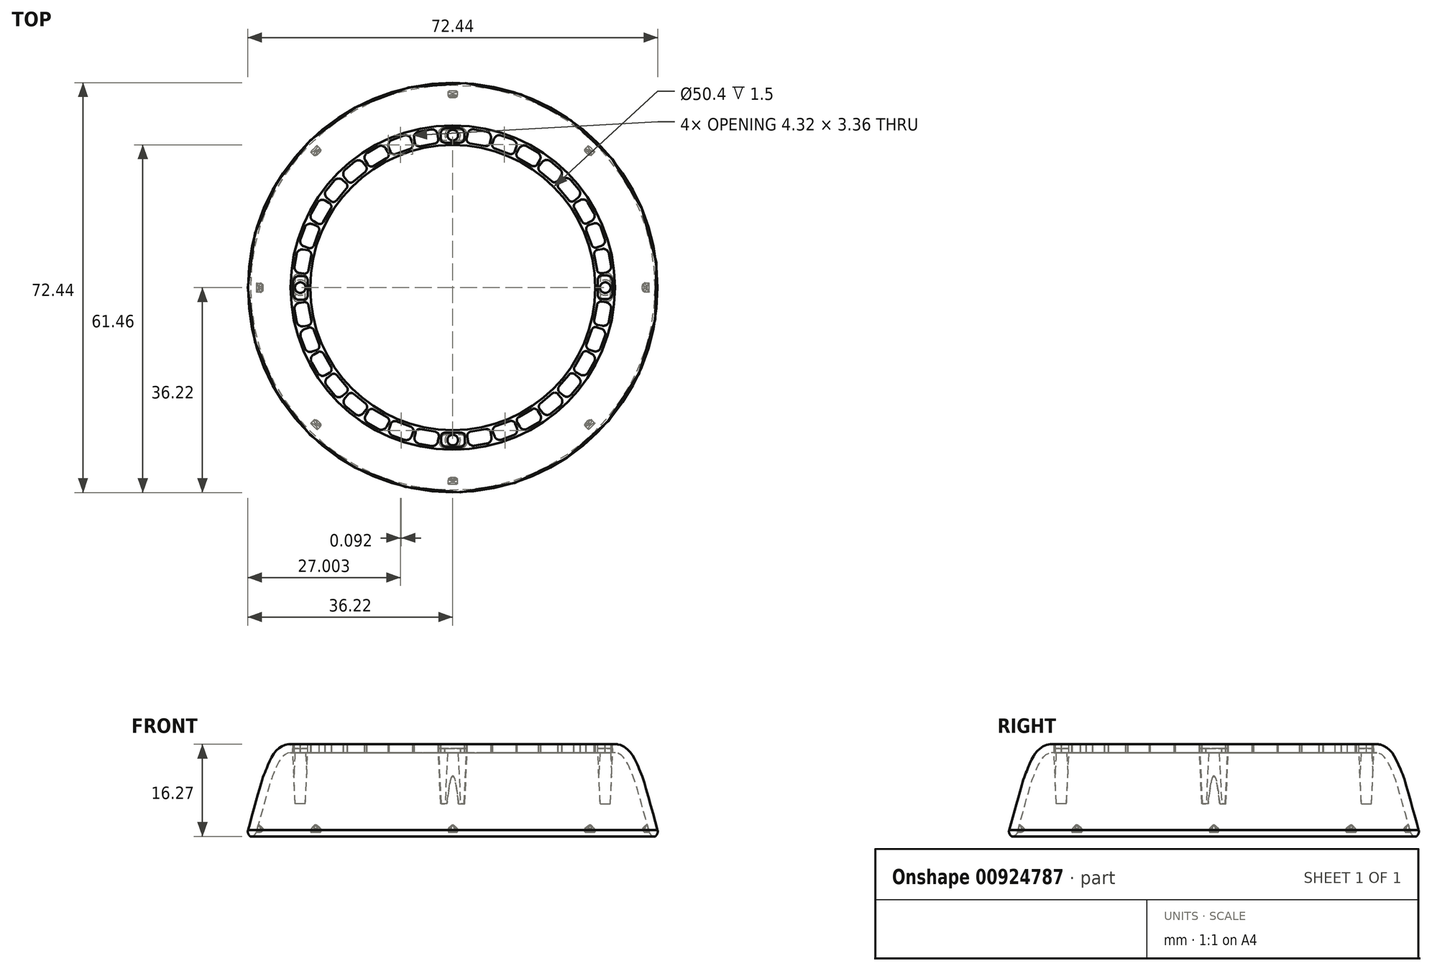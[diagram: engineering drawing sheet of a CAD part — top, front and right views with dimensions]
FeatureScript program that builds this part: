
annotation { "Feature Type Name" : "Feature", "Feature Type Description" : "" }
export const myFeature = defineFeature(function(context is Context, id is Id, definition is map)
    precondition{}
    {
        {
            var Q0;
            Q0=qCreatedBy(makeId("Front.planeOp"),FACE);
            var sketch = newSketch(context, id + "F0", { "sketchPlane" : qUnion([Q0])});
            skLineSegment(sketch, "E0", {"start": v(-25.2, 15) * mm, "end": v(-28.7, 15) * mm});
            skLineSegment(sketch, "E1", {"start": v(0, 0) * mm, "end": v(0, 15) * mm, "construction": true});
            skLineSegment(sketch, "E2", {"start": v(-25.2, 15) * mm, "end": v(0, 15) * mm, "construction": true});
            skLineSegment(sketch, "E3", {"start": v(0, 0) * mm, "end": v(-35, 0) * mm, "construction": true});
            skFitSpline(sketch, "E4", {"points": [v(-28.7, 15) * mm, v(-31.6, 11.48) * mm, v(-35, 0) * mm], "startDerivative": vector(-11.95, 0.53) * mm, "endDerivative": vector(-15.44, -55.66) * mm});
            skLineSegment(sketch, "E5", {"start": v(-25.2, 15) * mm, "end": v(-25.2, 0) * mm, "construction": true});
            skLineSegment(sketch, "E6", {"start": v(-25.2, 0) * mm, "end": v(-35, 0) * mm, "construction": true});
            skFitSpline(sketch, "E7.0", {"points": [v(-28.63, 16.5) * mm, v(-28.9, 16.51) * mm, v(-29.41, 16.46) * mm, v(-30.09, 16.2) * mm, v(-30.65, 15.85) * mm, v(-31.25, 15.3) * mm, v(-31.81, 14.54) * mm, v(-32.32, 13.61) * mm, v(-32.7, 12.75) * mm, v(-32.93, 12.16) * mm, v(-33.06, 11.85) * mm, v(-33.18, 11.58) * mm, v(-33.3, 11.3) * mm, v(-33.44, 10.94) * mm, v(-33.6, 10.49) * mm, v(-33.8, 9.88) * mm, v(-34.13, 8.7) * mm, v(-34.82, 6.27) * mm, v(-35.8, 2.72) * mm, v(-36.45, 0.4) * mm]});
            skLineSegment(sketch, "E7.1", {"start": v(-25.2, 16.5) * mm, "end": v(-28.67, 16.5) * mm});
            skLineSegment(sketch, "E8", {"start": v(-35.52, 0.14) * mm, "end": v(-36, 0.3) * mm});
            skLineSegment(sketch, "E9", {"start": v(-25.2, 16.5) * mm, "end": v(-25.2, 15) * mm});
            skArc(sketch, "E10.filletArc", {"start": v(-36, 0.3) * mm, "mid": v(-35.22, 0.36) * mm, "end": v(-34.73, 0.98) * mm});
            skPoint(sketch, "E11.visualSharp", {"position": v(-36.44, 0.43) * mm});
            skArc(sketch, "E11.filletArc", {"start": v(-36.18, 1.36) * mm, "mid": v(-36.1, 0.61) * mm, "end": v(-35.52, 0.14) * mm});
            skLineSegment(sketch, "E12", {"start": v(-25.2, 16.5) * mm, "end": v(0, 16.5) * mm, "construction": true});
            skLineSegment(sketch, "E13", {"start": v(0, 16.5) * mm, "end": v(0, 15) * mm, "construction": true});
            skLineSegment(sketch, "E14", {"start": v(-36.18, 1.36) * mm, "end": v(0, 1.36) * mm, "construction": true});
            skLineSegment(sketch, "E15.bottom", {"start": v(-25.7, 15) * mm, "end": v(-25.2, 15) * mm});
            skLineSegment(sketch, "E15.top", {"start": v(-25.45, 14.25) * mm, "end": v(-25.2, 14.25) * mm});
            skLineSegment(sketch, "E15.left", {"start": v(-25.7, 15) * mm, "end": v(-25.7, 14.5) * mm});
            skLineSegment(sketch, "E15.right", {"start": v(-25.2, 15) * mm, "end": v(-25.2, 14.25) * mm});
            skPoint(sketch, "E16.visualSharp", {"position": v(-25.7, 14.25) * mm});
            skArc(sketch, "E16.filletArc", {"start": v(-25.7, 14.5) * mm, "mid": v(-25.63, 14.32) * mm, "end": v(-25.45, 14.25) * mm});
            skSolve(sketch);
        }
        {
            var Q0;
            Q0=makeQuery(id+"F0.imprint","IMPRINT",FACE,{"disambiguationData":[TD([[makeQuery(id+"F0.imprint","IMPRINT",EDGE,{"derivedFrom":sQuery(id+"F0.wireOp",EDGE,"E0")}),-1.0]])]});
            var Q1;
            Q1=makeQuery(id+"F0.imprint","IMPRINT",FACE,{"disambiguationData":[TD([[makeQuery(id+"F0.imprint","IMPRINT",EDGE,{"derivedFrom":sQuery(id+"F0.wireOp",EDGE,"E15.bottom")}),-1.0]])]});
            var Q2;
            Q2=sQuery(id+"F0.wireOp",EDGE,"E1");
            revolve(context, id + "F1", {"surfaceOperationType" : NewSurfaceOperationType.NEW, "entities" : qUnion([Q0, Q1]), "axis" : qUnion([Q2]), "revolveType" : RevolveType.FULL});
        }
        {
            var Q0;
            Q0=sQuery(id+"F0.wireOp",VERTEX,"E1.end");
            var Q1;
            Q1=sQuery(id+"F0.wireOp",EDGE,"E1");
            cPlane(context, id + "F2", {"entities" : qUnion([Q0, Q1]), "cplaneType" : CPlaneType.LINE_POINT, "offset" : 25 * mm, "width" : 150 * mm, "height" : 150 * mm});
        }
        {
            var Q0;
            Q0=qCreatedBy(id+"F2.planeOp",FACE);
            var sketch = newSketch(context, id + "F3", { "sketchPlane" : qUnion([Q0])});
            skPoint(sketch, "E17.center", {"position": v(0, 0) * mm});
            skLineSegment(sketch, "E18.bottom", {"start": v(-27.26, -2.54) * mm, "end": v(-26.63, -2.54) * mm});
            skLineSegment(sketch, "E18.top", {"start": v(-27.26, 2.43) * mm, "end": v(-26.63, 2.43) * mm});
            skLineSegment(sketch, "E18.left", {"start": v(-28.26, -1.54) * mm, "end": v(-28.26, 1.43) * mm});
            skLineSegment(sketch, "E18.right", {"start": v(-25.63, -1.54) * mm, "end": v(-25.63, 1.43) * mm});
            skPoint(sketch, "E19.visualSharp", {"position": v(-28.26, 2.43) * mm});
            skArc(sketch, "E19.filletArc", {"start": v(-27.26, 2.43) * mm, "mid": v(-27.97, 2.13) * mm, "end": v(-28.26, 1.43) * mm});
            skPoint(sketch, "E20.visualSharp", {"position": v(-25.63, 2.43) * mm});
            skArc(sketch, "E20.filletArc", {"start": v(-25.63, 1.43) * mm, "mid": v(-25.92, 2.13) * mm, "end": v(-26.63, 2.43) * mm});
            skPoint(sketch, "E21.visualSharp", {"position": v(-28.26, -2.54) * mm});
            skArc(sketch, "E21.filletArc", {"start": v(-28.26, -1.54) * mm, "mid": v(-27.97, -2.25) * mm, "end": v(-27.26, -2.54) * mm});
            skPoint(sketch, "E22.visualSharp", {"position": v(-25.63, -2.54) * mm});
            skArc(sketch, "E22.filletArc", {"start": v(-26.63, -2.54) * mm, "mid": v(-25.92, -2.25) * mm, "end": v(-25.63, -1.54) * mm});
            skPoint(sketch, "E23.center", {"position": v(-0.04, -0.06) * mm});
            skLineSegment(sketch, "E24", {"start": v(-26.95, 2.43) * mm, "end": v(-26.95, -2.54) * mm, "construction": true});
            skLineSegment(sketch, "E25", {"start": v(-28.26, -0.06) * mm, "end": v(-25.63, -0.06) * mm, "construction": true});
            skCircle(sketch, "E26", {"center": v(-26.95, 0) * mm, "radius": 0.94 * mm});
            skPoint(sketch, "E26.centerSnap0", {"position": v(-26.95, -0.06) * mm});
            skLineSegment(sketch, "E27.left", {"start": v(-28.26, 0.46) * mm, "end": v(-28.26, -0.54) * mm});
            skSolve(sketch);
        }
        {
            var Q0;
            Q0 = qSketchRegion(id + "F3", true);
            extrude(context, id + "F4", {"entities" : qUnion([Q0]), "oppositeDirection" : true, "depth" : 9 * mm, "offsetDistance" : 25 * mm, "hasDraft" : true, "draftAngle" : 2.65 * degree, "draftPullDirection" : true, "hasSecondDirection" : true, "secondDirectionOppositeDirection" : false, "secondDirectionDepth" : .75 * mm});
        }
        {
            var Q0;
            Q0=sQuery(id+"F0.wireOp",VERTEX,"E12.end");
            var Q1;
            Q1=sQuery(id+"F0.wireOp",EDGE,"E13");
            cPlane(context, id + "F5", {"entities" : qUnion([Q0, Q1]), "cplaneType" : CPlaneType.LINE_POINT, "offset" : 25 * mm, "width" : 150 * mm, "height" : 150 * mm});
        }
        {
            var Q0;
            Q0=qCreatedBy(id+"F5.planeOp",FACE);
            var sketch = newSketch(context, id + "F6", { "sketchPlane" : qUnion([Q0])});
            skLineSegment(sketch, "E28", {"start": v(-25.63, -1.3) * mm, "end": v(-25.63, 1.4) * mm});
            skLineSegment(sketch, "E29", {"start": v(-26.38, 2.14) * mm, "end": v(-27.2, 2.14) * mm});
            skLineSegment(sketch, "E30", {"start": v(-28.2, 1.14) * mm, "end": v(-28.2, -1.05) * mm});
            skLineSegment(sketch, "E31", {"start": v(-27.2, -2.05) * mm, "end": v(-26.38, -2.05) * mm});
            skPoint(sketch, "E32.visualSharp", {"position": v(-28.2, -2.05) * mm});
            skArc(sketch, "E32.filletArc", {"start": v(-28.2, -1.05) * mm, "mid": v(-27.91, -1.75) * mm, "end": v(-27.2, -2.05) * mm});
            skPoint(sketch, "E33.visualSharp", {"position": v(-25.63, -2.05) * mm});
            skArc(sketch, "E33.filletArc", {"start": v(-26.38, -2.05) * mm, "mid": v(-25.85, -1.83) * mm, "end": v(-25.63, -1.3) * mm});
            skPoint(sketch, "E34.visualSharp", {"position": v(-25.63, 2.14) * mm});
            skArc(sketch, "E34.filletArc", {"start": v(-25.63, 1.4) * mm, "mid": v(-25.85, 1.92) * mm, "end": v(-26.38, 2.14) * mm});
            skPoint(sketch, "E35.visualSharp", {"position": v(-28.2, 2.14) * mm});
            skArc(sketch, "E35.filletArc", {"start": v(-27.2, 2.14) * mm, "mid": v(-27.91, 1.85) * mm, "end": v(-28.2, 1.14) * mm});
            skPoint(sketch, "E36.1.0", {"position": v(-25.61, -2.34) * mm});
            skArc(sketch, "E36.1.1", {"start": v(-27.16, -2.61) * mm, "mid": v(-27.8, -3.02) * mm, "end": v(-27.97, -3.77) * mm});
            skLineSegment(sketch, "E36.1.2", {"start": v(-26.43, -6.74) * mm, "end": v(-25.62, -6.6) * mm});
            skArc(sketch, "E36.1.3", {"start": v(-25.62, -6.6) * mm, "mid": v(-25.14, -6.29) * mm, "end": v(-25.01, -5.73) * mm});
            skArc(sketch, "E36.1.4", {"start": v(-25.48, -3.08) * mm, "mid": v(-25.79, -2.6) * mm, "end": v(-26.35, -2.47) * mm});
            skPoint(sketch, "E36.1.5", {"position": v(-27.42, -6.91) * mm});
            skArc(sketch, "E36.1.6", {"start": v(-27.6, -5.93) * mm, "mid": v(-27.18, -6.57) * mm, "end": v(-26.43, -6.74) * mm});
            skPoint(sketch, "E36.1.7", {"position": v(-28.15, -2.79) * mm});
            skLineSegment(sketch, "E36.1.8", {"start": v(-25.01, -5.73) * mm, "end": v(-25.48, -3.08) * mm});
            skPoint(sketch, "E36.1.9", {"position": v(-24.88, -6.47) * mm});
            skLineSegment(sketch, "E36.1.10", {"start": v(-26.35, -2.47) * mm, "end": v(-27.16, -2.61) * mm});
            skLineSegment(sketch, "E36.1.11", {"start": v(-27.97, -3.77) * mm, "end": v(-27.6, -5.93) * mm});
            skPoint(sketch, "E36.2.0", {"position": v(-24.82, -6.75) * mm});
            skArc(sketch, "E36.2.1", {"start": v(-26.3, -7.29) * mm, "mid": v(-26.86, -7.8) * mm, "end": v(-26.9, -8.57) * mm});
            skLineSegment(sketch, "E36.2.2", {"start": v(-24.86, -11.23) * mm, "end": v(-24.09, -10.94) * mm});
            skArc(sketch, "E36.2.3", {"start": v(-24.09, -10.94) * mm, "mid": v(-23.66, -10.56) * mm, "end": v(-23.64, -9.98) * mm});
            skArc(sketch, "E36.2.4", {"start": v(-24.56, -7.45) * mm, "mid": v(-24.95, -7.03) * mm, "end": v(-25.52, -7) * mm});
            skPoint(sketch, "E36.2.5", {"position": v(-25.8, -11.57) * mm});
            skArc(sketch, "E36.2.6", {"start": v(-26.14, -10.63) * mm, "mid": v(-25.63, -11.2) * mm, "end": v(-24.86, -11.23) * mm});
            skPoint(sketch, "E36.2.7", {"position": v(-27.24, -7.63) * mm});
            skLineSegment(sketch, "E36.2.8", {"start": v(-23.64, -9.98) * mm, "end": v(-24.56, -7.45) * mm});
            skPoint(sketch, "E36.2.9", {"position": v(-23.38, -10.69) * mm});
            skLineSegment(sketch, "E36.2.10", {"start": v(-25.52, -7) * mm, "end": v(-26.3, -7.29) * mm});
            skLineSegment(sketch, "E36.2.11", {"start": v(-26.9, -8.57) * mm, "end": v(-26.14, -10.63) * mm});
            skPoint(sketch, "E36.3.0", {"position": v(-23.27, -10.96) * mm});
            skArc(sketch, "E36.3.1", {"start": v(-24.63, -11.74) * mm, "mid": v(-25.1, -12.35) * mm, "end": v(-25, -13.11) * mm});
            skLineSegment(sketch, "E36.3.2", {"start": v(-22.54, -15.37) * mm, "end": v(-21.82, -14.96) * mm});
            skArc(sketch, "E36.3.3", {"start": v(-21.82, -14.96) * mm, "mid": v(-21.47, -14.5) * mm, "end": v(-21.55, -13.94) * mm});
            skArc(sketch, "E36.3.4", {"start": v(-22.9, -11.6) * mm, "mid": v(-23.35, -11.26) * mm, "end": v(-23.92, -11.33) * mm});
            skPoint(sketch, "E36.3.5", {"position": v(-23.4, -15.87) * mm});
            skArc(sketch, "E36.3.6", {"start": v(-23.9, -15) * mm, "mid": v(-23.3, -15.47) * mm, "end": v(-22.54, -15.37) * mm});
            skPoint(sketch, "E36.3.7", {"position": v(-25.5, -12.24) * mm});
            skLineSegment(sketch, "E36.3.8", {"start": v(-21.55, -13.94) * mm, "end": v(-22.9, -11.6) * mm});
            skPoint(sketch, "E36.3.9", {"position": v(-21.17, -14.59) * mm});
            skLineSegment(sketch, "E36.3.10", {"start": v(-23.92, -11.33) * mm, "end": v(-24.63, -11.74) * mm});
            skLineSegment(sketch, "E36.3.11", {"start": v(-25, -13.11) * mm, "end": v(-23.9, -15) * mm});
            skPoint(sketch, "E36.4.0", {"position": v(-21.01, -14.83) * mm});
            skArc(sketch, "E36.4.1", {"start": v(-22.22, -15.84) * mm, "mid": v(-22.57, -16.52) * mm, "end": v(-22.34, -17.25) * mm});
            skLineSegment(sketch, "E36.4.2", {"start": v(-19.52, -19.05) * mm, "end": v(-18.9, -18.52) * mm});
            skArc(sketch, "E36.4.3", {"start": v(-18.9, -18.52) * mm, "mid": v(-18.63, -18.01) * mm, "end": v(-18.8, -17.47) * mm});
            skArc(sketch, "E36.4.4", {"start": v(-20.53, -15.4) * mm, "mid": v(-21.04, -15.14) * mm, "end": v(-21.59, -15.31) * mm});
            skPoint(sketch, "E36.4.5", {"position": v(-20.29, -19.7) * mm});
            skArc(sketch, "E36.4.6", {"start": v(-20.93, -18.93) * mm, "mid": v(-20.25, -19.28) * mm, "end": v(-19.52, -19.05) * mm});
            skPoint(sketch, "E36.4.7", {"position": v(-22.98, -16.49) * mm});
            skLineSegment(sketch, "E36.4.8", {"start": v(-18.8, -17.47) * mm, "end": v(-20.53, -15.4) * mm});
            skPoint(sketch, "E36.4.9", {"position": v(-18.32, -18.04) * mm});
            skLineSegment(sketch, "E36.4.10", {"start": v(-21.59, -15.31) * mm, "end": v(-22.22, -15.84) * mm});
            skLineSegment(sketch, "E36.4.11", {"start": v(-22.34, -17.25) * mm, "end": v(-20.93, -18.93) * mm});
            skPoint(sketch, "E36.5.0", {"position": v(-18.12, -18.25) * mm});
            skArc(sketch, "E36.5.1", {"start": v(-19.13, -19.46) * mm, "mid": v(-19.36, -20.2) * mm, "end": v(-19, -20.87) * mm});
            skLineSegment(sketch, "E36.5.2", {"start": v(-15.92, -22.15) * mm, "end": v(-15.39, -21.52) * mm});
            skArc(sketch, "E36.5.3", {"start": v(-15.39, -21.52) * mm, "mid": v(-15.22, -20.97) * mm, "end": v(-15.48, -20.47) * mm});
            skArc(sketch, "E36.5.4", {"start": v(-17.54, -18.74) * mm, "mid": v(-18.09, -18.56) * mm, "end": v(-18.6, -18.83) * mm});
            skPoint(sketch, "E36.5.5", {"position": v(-16.56, -22.92) * mm});
            skArc(sketch, "E36.5.6", {"start": v(-17.33, -22.28) * mm, "mid": v(-16.6, -22.5) * mm, "end": v(-15.92, -22.15) * mm});
            skPoint(sketch, "E36.5.7", {"position": v(-19.77, -20.23) * mm});
            skLineSegment(sketch, "E36.5.8", {"start": v(-15.48, -20.47) * mm, "end": v(-17.54, -18.74) * mm});
            skPoint(sketch, "E36.5.9", {"position": v(-14.9, -20.95) * mm});
            skLineSegment(sketch, "E36.5.10", {"start": v(-18.6, -18.83) * mm, "end": v(-19.13, -19.46) * mm});
            skLineSegment(sketch, "E36.5.11", {"start": v(-19, -20.87) * mm, "end": v(-17.33, -22.28) * mm});
            skPoint(sketch, "E36.6.0", {"position": v(-14.67, -21.12) * mm});
            skArc(sketch, "E36.6.1", {"start": v(-15.46, -22.49) * mm, "mid": v(-15.56, -23.25) * mm, "end": v(-15.1, -23.85) * mm});
            skLineSegment(sketch, "E36.6.2", {"start": v(-11.83, -24.58) * mm, "end": v(-11.42, -23.87) * mm});
            skArc(sketch, "E36.6.3", {"start": v(-11.42, -23.87) * mm, "mid": v(-11.34, -23.3) * mm, "end": v(-11.7, -22.84) * mm});
            skArc(sketch, "E36.6.4", {"start": v(-14.02, -21.5) * mm, "mid": v(-14.6, -21.42) * mm, "end": v(-15.05, -21.77) * mm});
            skPoint(sketch, "E36.6.5", {"position": v(-12.33, -25.45) * mm});
            skArc(sketch, "E36.6.6", {"start": v(-13.2, -24.95) * mm, "mid": v(-12.44, -25.05) * mm, "end": v(-11.83, -24.58) * mm});
            skPoint(sketch, "E36.6.7", {"position": v(-15.96, -23.35) * mm});
            skLineSegment(sketch, "E36.6.8", {"start": v(-11.7, -22.84) * mm, "end": v(-14.02, -21.5) * mm});
            skPoint(sketch, "E36.6.9", {"position": v(-11.04, -23.22) * mm});
            skLineSegment(sketch, "E36.6.10", {"start": v(-15.05, -21.77) * mm, "end": v(-15.46, -22.49) * mm});
            skLineSegment(sketch, "E36.6.11", {"start": v(-15.1, -23.85) * mm, "end": v(-13.2, -24.95) * mm});
            skPoint(sketch, "E36.7.0", {"position": v(-10.78, -23.35) * mm});
            skArc(sketch, "E36.7.1", {"start": v(-11.32, -24.83) * mm, "mid": v(-11.29, -25.6) * mm, "end": v(-10.72, -26.11) * mm});
            skLineSegment(sketch, "E36.7.2", {"start": v(-7.38, -26.26) * mm, "end": v(-7.1, -25.49) * mm});
            skArc(sketch, "E36.7.3", {"start": v(-7.1, -25.49) * mm, "mid": v(-7.12, -24.91) * mm, "end": v(-7.55, -24.53) * mm});
            skArc(sketch, "E36.7.4", {"start": v(-10.08, -23.6) * mm, "mid": v(-10.65, -23.63) * mm, "end": v(-11.04, -24.05) * mm});
            skPoint(sketch, "E36.7.5", {"position": v(-7.72, -27.2) * mm});
            skArc(sketch, "E36.7.6", {"start": v(-8.66, -26.86) * mm, "mid": v(-7.9, -26.83) * mm, "end": v(-7.38, -26.26) * mm});
            skPoint(sketch, "E36.7.7", {"position": v(-11.66, -25.77) * mm});
            skLineSegment(sketch, "E36.7.8", {"start": v(-7.55, -24.53) * mm, "end": v(-10.08, -23.6) * mm});
            skPoint(sketch, "E36.7.9", {"position": v(-6.84, -24.78) * mm});
            skLineSegment(sketch, "E36.7.10", {"start": v(-11.04, -24.05) * mm, "end": v(-11.32, -24.83) * mm});
            skLineSegment(sketch, "E36.7.11", {"start": v(-10.72, -26.11) * mm, "end": v(-8.66, -26.86) * mm});
            skPoint(sketch, "E36.8.0", {"position": v(-6.56, -24.87) * mm});
            skArc(sketch, "E36.8.1", {"start": v(-6.84, -26.42) * mm, "mid": v(-6.67, -27.17) * mm, "end": v(-6.02, -27.58) * mm});
            skLineSegment(sketch, "E36.8.2", {"start": v(-2.7, -27.15) * mm, "end": v(-2.57, -26.33) * mm});
            skArc(sketch, "E36.8.3", {"start": v(-2.57, -26.33) * mm, "mid": v(-2.69, -25.77) * mm, "end": v(-3.17, -25.46) * mm});
            skArc(sketch, "E36.8.4", {"start": v(-5.82, -25) * mm, "mid": v(-6.38, -25.12) * mm, "end": v(-6.7, -25.6) * mm});
            skPoint(sketch, "E36.8.5", {"position": v(-2.88, -28.13) * mm});
            skArc(sketch, "E36.8.6", {"start": v(-3.87, -27.96) * mm, "mid": v(-3.12, -27.8) * mm, "end": v(-2.7, -27.15) * mm});
            skPoint(sketch, "E36.8.7", {"position": v(-7, -27.4) * mm});
            skLineSegment(sketch, "E36.8.8", {"start": v(-3.17, -25.46) * mm, "end": v(-5.82, -25) * mm});
            skPoint(sketch, "E36.8.9", {"position": v(-2.43, -25.6) * mm});
            skLineSegment(sketch, "E36.8.10", {"start": v(-6.7, -25.6) * mm, "end": v(-6.84, -26.42) * mm});
            skLineSegment(sketch, "E36.8.11", {"start": v(-6.02, -27.58) * mm, "end": v(-3.87, -27.96) * mm});
            skPoint(sketch, "E36.9.0", {"position": v(-2.14, -25.63) * mm});
            skArc(sketch, "E36.9.1", {"start": v(-2.14, -27.2) * mm, "mid": v(-1.85, -27.91) * mm, "end": v(-1.14, -28.2) * mm});
            skLineSegment(sketch, "E36.9.2", {"start": v(2.05, -27.2) * mm, "end": v(2.05, -26.38) * mm});
            skArc(sketch, "E36.9.3", {"start": v(2.05, -26.38) * mm, "mid": v(1.83, -25.85) * mm, "end": v(1.3, -25.63) * mm});
            skArc(sketch, "E36.9.4", {"start": v(-1.4, -25.63) * mm, "mid": v(-1.92, -25.85) * mm, "end": v(-2.14, -26.38) * mm});
            skPoint(sketch, "E36.9.5", {"position": v(2.05, -28.2) * mm});
            skArc(sketch, "E36.9.6", {"start": v(1.05, -28.2) * mm, "mid": v(1.75, -27.91) * mm, "end": v(2.05, -27.2) * mm});
            skPoint(sketch, "E36.9.7", {"position": v(-2.14, -28.2) * mm});
            skLineSegment(sketch, "E36.9.8", {"start": v(1.3, -25.63) * mm, "end": v(-1.4, -25.63) * mm});
            skPoint(sketch, "E36.9.9", {"position": v(2.05, -25.63) * mm});
            skLineSegment(sketch, "E36.9.10", {"start": v(-2.14, -26.38) * mm, "end": v(-2.14, -27.2) * mm});
            skLineSegment(sketch, "E36.9.11", {"start": v(-1.14, -28.2) * mm, "end": v(1.05, -28.2) * mm});
            skPoint(sketch, "E36.10.0", {"position": v(2.34, -25.61) * mm});
            skArc(sketch, "E36.10.1", {"start": v(2.61, -27.16) * mm, "mid": v(3.02, -27.8) * mm, "end": v(3.77, -27.97) * mm});
            skLineSegment(sketch, "E36.10.2", {"start": v(6.74, -26.43) * mm, "end": v(6.6, -25.62) * mm});
            skArc(sketch, "E36.10.3", {"start": v(6.6, -25.62) * mm, "mid": v(6.29, -25.14) * mm, "end": v(5.73, -25.01) * mm});
            skArc(sketch, "E36.10.4", {"start": v(3.08, -25.48) * mm, "mid": v(2.6, -25.79) * mm, "end": v(2.47, -26.35) * mm});
            skPoint(sketch, "E36.10.5", {"position": v(6.91, -27.42) * mm});
            skArc(sketch, "E36.10.6", {"start": v(5.93, -27.6) * mm, "mid": v(6.57, -27.18) * mm, "end": v(6.74, -26.43) * mm});
            skPoint(sketch, "E36.10.7", {"position": v(2.79, -28.15) * mm});
            skLineSegment(sketch, "E36.10.8", {"start": v(5.73, -25.01) * mm, "end": v(3.08, -25.48) * mm});
            skPoint(sketch, "E36.10.9", {"position": v(6.47, -24.88) * mm});
            skLineSegment(sketch, "E36.10.10", {"start": v(2.47, -26.35) * mm, "end": v(2.61, -27.16) * mm});
            skLineSegment(sketch, "E36.10.11", {"start": v(3.77, -27.97) * mm, "end": v(5.93, -27.6) * mm});
            skPoint(sketch, "E36.11.0", {"position": v(6.75, -24.82) * mm});
            skArc(sketch, "E36.11.1", {"start": v(7.29, -26.3) * mm, "mid": v(7.8, -26.86) * mm, "end": v(8.57, -26.9) * mm});
            skLineSegment(sketch, "E36.11.2", {"start": v(11.23, -24.86) * mm, "end": v(10.94, -24.09) * mm});
            skArc(sketch, "E36.11.3", {"start": v(10.94, -24.09) * mm, "mid": v(10.56, -23.66) * mm, "end": v(9.98, -23.64) * mm});
            skArc(sketch, "E36.11.4", {"start": v(7.45, -24.56) * mm, "mid": v(7.03, -24.95) * mm, "end": v(7, -25.52) * mm});
            skPoint(sketch, "E36.11.5", {"position": v(11.57, -25.8) * mm});
            skArc(sketch, "E36.11.6", {"start": v(10.63, -26.14) * mm, "mid": v(11.2, -25.63) * mm, "end": v(11.23, -24.86) * mm});
            skPoint(sketch, "E36.11.7", {"position": v(7.63, -27.24) * mm});
            skLineSegment(sketch, "E36.11.8", {"start": v(9.98, -23.64) * mm, "end": v(7.45, -24.56) * mm});
            skPoint(sketch, "E36.11.9", {"position": v(10.69, -23.38) * mm});
            skLineSegment(sketch, "E36.11.10", {"start": v(7, -25.52) * mm, "end": v(7.29, -26.3) * mm});
            skLineSegment(sketch, "E36.11.11", {"start": v(8.57, -26.9) * mm, "end": v(10.63, -26.14) * mm});
            skPoint(sketch, "E36.12.0", {"position": v(10.96, -23.27) * mm});
            skArc(sketch, "E36.12.1", {"start": v(11.74, -24.63) * mm, "mid": v(12.35, -25.1) * mm, "end": v(13.11, -25) * mm});
            skLineSegment(sketch, "E36.12.2", {"start": v(15.37, -22.54) * mm, "end": v(14.96, -21.82) * mm});
            skArc(sketch, "E36.12.3", {"start": v(14.96, -21.82) * mm, "mid": v(14.5, -21.47) * mm, "end": v(13.94, -21.55) * mm});
            skArc(sketch, "E36.12.4", {"start": v(11.6, -22.9) * mm, "mid": v(11.26, -23.35) * mm, "end": v(11.33, -23.92) * mm});
            skPoint(sketch, "E36.12.5", {"position": v(15.87, -23.4) * mm});
            skArc(sketch, "E36.12.6", {"start": v(15, -23.9) * mm, "mid": v(15.47, -23.3) * mm, "end": v(15.37, -22.54) * mm});
            skPoint(sketch, "E36.12.7", {"position": v(12.24, -25.5) * mm});
            skLineSegment(sketch, "E36.12.8", {"start": v(13.94, -21.55) * mm, "end": v(11.6, -22.9) * mm});
            skPoint(sketch, "E36.12.9", {"position": v(14.59, -21.17) * mm});
            skLineSegment(sketch, "E36.12.10", {"start": v(11.33, -23.92) * mm, "end": v(11.74, -24.63) * mm});
            skLineSegment(sketch, "E36.12.11", {"start": v(13.11, -25) * mm, "end": v(15, -23.9) * mm});
            skPoint(sketch, "E36.13.0", {"position": v(14.83, -21.01) * mm});
            skArc(sketch, "E36.13.1", {"start": v(15.84, -22.22) * mm, "mid": v(16.52, -22.57) * mm, "end": v(17.25, -22.34) * mm});
            skLineSegment(sketch, "E36.13.2", {"start": v(19.05, -19.52) * mm, "end": v(18.52, -18.9) * mm});
            skArc(sketch, "E36.13.3", {"start": v(18.52, -18.9) * mm, "mid": v(18.01, -18.63) * mm, "end": v(17.47, -18.8) * mm});
            skArc(sketch, "E36.13.4", {"start": v(15.4, -20.53) * mm, "mid": v(15.14, -21.04) * mm, "end": v(15.31, -21.59) * mm});
            skPoint(sketch, "E36.13.5", {"position": v(19.7, -20.29) * mm});
            skArc(sketch, "E36.13.6", {"start": v(18.93, -20.93) * mm, "mid": v(19.28, -20.25) * mm, "end": v(19.05, -19.52) * mm});
            skPoint(sketch, "E36.13.7", {"position": v(16.49, -22.98) * mm});
            skLineSegment(sketch, "E36.13.8", {"start": v(17.47, -18.8) * mm, "end": v(15.4, -20.53) * mm});
            skPoint(sketch, "E36.13.9", {"position": v(18.04, -18.32) * mm});
            skLineSegment(sketch, "E36.13.10", {"start": v(15.31, -21.59) * mm, "end": v(15.84, -22.22) * mm});
            skLineSegment(sketch, "E36.13.11", {"start": v(17.25, -22.34) * mm, "end": v(18.93, -20.93) * mm});
            skPoint(sketch, "E36.14.0", {"position": v(18.25, -18.12) * mm});
            skArc(sketch, "E36.14.1", {"start": v(19.46, -19.13) * mm, "mid": v(20.2, -19.36) * mm, "end": v(20.87, -19) * mm});
            skLineSegment(sketch, "E36.14.2", {"start": v(22.15, -15.92) * mm, "end": v(21.52, -15.39) * mm});
            skArc(sketch, "E36.14.3", {"start": v(21.52, -15.39) * mm, "mid": v(20.97, -15.22) * mm, "end": v(20.47, -15.48) * mm});
            skArc(sketch, "E36.14.4", {"start": v(18.74, -17.54) * mm, "mid": v(18.56, -18.09) * mm, "end": v(18.83, -18.6) * mm});
            skPoint(sketch, "E36.14.5", {"position": v(22.92, -16.56) * mm});
            skArc(sketch, "E36.14.6", {"start": v(22.28, -17.33) * mm, "mid": v(22.5, -16.6) * mm, "end": v(22.15, -15.92) * mm});
            skPoint(sketch, "E36.14.7", {"position": v(20.23, -19.77) * mm});
            skLineSegment(sketch, "E36.14.8", {"start": v(20.47, -15.48) * mm, "end": v(18.74, -17.54) * mm});
            skPoint(sketch, "E36.14.9", {"position": v(20.95, -14.9) * mm});
            skLineSegment(sketch, "E36.14.10", {"start": v(18.83, -18.6) * mm, "end": v(19.46, -19.13) * mm});
            skLineSegment(sketch, "E36.14.11", {"start": v(20.87, -19) * mm, "end": v(22.28, -17.33) * mm});
            skPoint(sketch, "E36.15.0", {"position": v(21.12, -14.67) * mm});
            skArc(sketch, "E36.15.1", {"start": v(22.49, -15.46) * mm, "mid": v(23.25, -15.56) * mm, "end": v(23.85, -15.1) * mm});
            skLineSegment(sketch, "E36.15.2", {"start": v(24.58, -11.83) * mm, "end": v(23.87, -11.42) * mm});
            skArc(sketch, "E36.15.3", {"start": v(23.87, -11.42) * mm, "mid": v(23.3, -11.34) * mm, "end": v(22.84, -11.7) * mm});
            skArc(sketch, "E36.15.4", {"start": v(21.5, -14.02) * mm, "mid": v(21.42, -14.6) * mm, "end": v(21.77, -15.05) * mm});
            skPoint(sketch, "E36.15.5", {"position": v(25.45, -12.33) * mm});
            skArc(sketch, "E36.15.6", {"start": v(24.95, -13.2) * mm, "mid": v(25.05, -12.44) * mm, "end": v(24.58, -11.83) * mm});
            skPoint(sketch, "E36.15.7", {"position": v(23.35, -15.96) * mm});
            skLineSegment(sketch, "E36.15.8", {"start": v(22.84, -11.7) * mm, "end": v(21.5, -14.02) * mm});
            skPoint(sketch, "E36.15.9", {"position": v(23.22, -11.04) * mm});
            skLineSegment(sketch, "E36.15.10", {"start": v(21.77, -15.05) * mm, "end": v(22.49, -15.46) * mm});
            skLineSegment(sketch, "E36.15.11", {"start": v(23.85, -15.1) * mm, "end": v(24.95, -13.2) * mm});
            skPoint(sketch, "E36.center", {"position": v(0, 0) * mm});
            skPoint(sketch, "E37.0.16.0", {"position": v(27.2, -7.72) * mm});
            skArc(sketch, "E37.1.16.0", {"start": v(24.83, -11.32) * mm, "mid": v(25.6, -11.29) * mm, "end": v(26.11, -10.72) * mm});
            skLineSegment(sketch, "E37.5.16.0", {"start": v(26.26, -7.38) * mm, "end": v(25.49, -7.1) * mm});
            skArc(sketch, "E37.8.16.0", {"start": v(25.49, -7.1) * mm, "mid": v(24.91, -7.12) * mm, "end": v(24.53, -7.55) * mm});
            skArc(sketch, "E37.12.16.0", {"start": v(23.6, -10.08) * mm, "mid": v(23.63, -10.65) * mm, "end": v(24.05, -11.04) * mm});
            skPoint(sketch, "E37.16.16.0", {"position": v(23.35, -10.78) * mm});
            skArc(sketch, "E37.17.16.0", {"start": v(26.86, -8.66) * mm, "mid": v(26.83, -7.9) * mm, "end": v(26.26, -7.38) * mm});
            skPoint(sketch, "E37.21.16.0", {"position": v(25.77, -11.66) * mm});
            skLineSegment(sketch, "E37.22.16.0", {"start": v(24.53, -7.55) * mm, "end": v(23.6, -10.08) * mm});
            skPoint(sketch, "E37.25.16.0", {"position": v(24.78, -6.84) * mm});
            skLineSegment(sketch, "E37.26.16.0", {"start": v(24.05, -11.04) * mm, "end": v(24.83, -11.32) * mm});
            skLineSegment(sketch, "E37.29.16.0", {"start": v(26.11, -10.72) * mm, "end": v(26.86, -8.66) * mm});
            skPoint(sketch, "E37.0.17.0", {"position": v(28.13, -2.88) * mm});
            skArc(sketch, "E37.1.17.0", {"start": v(26.42, -6.84) * mm, "mid": v(27.17, -6.67) * mm, "end": v(27.58, -6.02) * mm});
            skLineSegment(sketch, "E37.5.17.0", {"start": v(27.15, -2.7) * mm, "end": v(26.33, -2.57) * mm});
            skArc(sketch, "E37.8.17.0", {"start": v(26.33, -2.57) * mm, "mid": v(25.77, -2.69) * mm, "end": v(25.46, -3.17) * mm});
            skArc(sketch, "E37.12.17.0", {"start": v(25, -5.82) * mm, "mid": v(25.12, -6.38) * mm, "end": v(25.6, -6.7) * mm});
            skPoint(sketch, "E37.16.17.0", {"position": v(24.87, -6.56) * mm});
            skArc(sketch, "E37.17.17.0", {"start": v(27.96, -3.87) * mm, "mid": v(27.8, -3.12) * mm, "end": v(27.15, -2.7) * mm});
            skPoint(sketch, "E37.21.17.0", {"position": v(27.4, -7) * mm});
            skLineSegment(sketch, "E37.22.17.0", {"start": v(25.46, -3.17) * mm, "end": v(25, -5.82) * mm});
            skPoint(sketch, "E37.25.17.0", {"position": v(25.6, -2.43) * mm});
            skLineSegment(sketch, "E37.26.17.0", {"start": v(25.6, -6.7) * mm, "end": v(26.42, -6.84) * mm});
            skLineSegment(sketch, "E37.29.17.0", {"start": v(27.58, -6.02) * mm, "end": v(27.96, -3.87) * mm});
            skPoint(sketch, "E37.0.18.0", {"position": v(28.2, 2.05) * mm});
            skArc(sketch, "E37.1.18.0", {"start": v(27.2, -2.14) * mm, "mid": v(27.91, -1.85) * mm, "end": v(28.2, -1.14) * mm});
            skLineSegment(sketch, "E37.5.18.0", {"start": v(27.2, 2.05) * mm, "end": v(26.38, 2.05) * mm});
            skArc(sketch, "E37.8.18.0", {"start": v(26.38, 2.05) * mm, "mid": v(25.85, 1.83) * mm, "end": v(25.63, 1.3) * mm});
            skArc(sketch, "E37.12.18.0", {"start": v(25.63, -1.4) * mm, "mid": v(25.85, -1.92) * mm, "end": v(26.38, -2.14) * mm});
            skPoint(sketch, "E37.16.18.0", {"position": v(25.63, -2.14) * mm});
            skArc(sketch, "E37.17.18.0", {"start": v(28.2, 1.05) * mm, "mid": v(27.91, 1.75) * mm, "end": v(27.2, 2.05) * mm});
            skPoint(sketch, "E37.21.18.0", {"position": v(28.2, -2.14) * mm});
            skLineSegment(sketch, "E37.22.18.0", {"start": v(25.63, 1.3) * mm, "end": v(25.63, -1.4) * mm});
            skPoint(sketch, "E37.25.18.0", {"position": v(25.63, 2.05) * mm});
            skLineSegment(sketch, "E37.26.18.0", {"start": v(26.38, -2.14) * mm, "end": v(27.2, -2.14) * mm});
            skLineSegment(sketch, "E37.29.18.0", {"start": v(28.2, -1.14) * mm, "end": v(28.2, 1.05) * mm});
            skPoint(sketch, "E37.0.19.0", {"position": v(27.42, 6.91) * mm});
            skArc(sketch, "E37.1.19.0", {"start": v(27.16, 2.61) * mm, "mid": v(27.8, 3.02) * mm, "end": v(27.97, 3.77) * mm});
            skLineSegment(sketch, "E37.5.19.0", {"start": v(26.43, 6.74) * mm, "end": v(25.62, 6.6) * mm});
            skArc(sketch, "E37.8.19.0", {"start": v(25.62, 6.6) * mm, "mid": v(25.14, 6.29) * mm, "end": v(25.01, 5.73) * mm});
            skArc(sketch, "E37.12.19.0", {"start": v(25.48, 3.08) * mm, "mid": v(25.79, 2.6) * mm, "end": v(26.35, 2.47) * mm});
            skPoint(sketch, "E37.16.19.0", {"position": v(25.61, 2.34) * mm});
            skArc(sketch, "E37.17.19.0", {"start": v(27.6, 5.93) * mm, "mid": v(27.18, 6.57) * mm, "end": v(26.43, 6.74) * mm});
            skPoint(sketch, "E37.21.19.0", {"position": v(28.15, 2.79) * mm});
            skLineSegment(sketch, "E37.22.19.0", {"start": v(25.01, 5.73) * mm, "end": v(25.48, 3.08) * mm});
            skPoint(sketch, "E37.25.19.0", {"position": v(24.88, 6.47) * mm});
            skLineSegment(sketch, "E37.26.19.0", {"start": v(26.35, 2.47) * mm, "end": v(27.16, 2.61) * mm});
            skLineSegment(sketch, "E37.29.19.0", {"start": v(27.97, 3.77) * mm, "end": v(27.6, 5.93) * mm});
            skPoint(sketch, "E37.0.20.0", {"position": v(25.8, 11.57) * mm});
            skArc(sketch, "E37.1.20.0", {"start": v(26.3, 7.29) * mm, "mid": v(26.86, 7.8) * mm, "end": v(26.9, 8.57) * mm});
            skLineSegment(sketch, "E37.5.20.0", {"start": v(24.86, 11.23) * mm, "end": v(24.09, 10.94) * mm});
            skArc(sketch, "E37.8.20.0", {"start": v(24.09, 10.94) * mm, "mid": v(23.66, 10.56) * mm, "end": v(23.64, 9.98) * mm});
            skArc(sketch, "E37.12.20.0", {"start": v(24.56, 7.45) * mm, "mid": v(24.95, 7.03) * mm, "end": v(25.52, 7) * mm});
            skPoint(sketch, "E37.16.20.0", {"position": v(24.82, 6.75) * mm});
            skArc(sketch, "E37.17.20.0", {"start": v(26.14, 10.63) * mm, "mid": v(25.63, 11.2) * mm, "end": v(24.86, 11.23) * mm});
            skPoint(sketch, "E37.21.20.0", {"position": v(27.24, 7.63) * mm});
            skLineSegment(sketch, "E37.22.20.0", {"start": v(23.64, 9.98) * mm, "end": v(24.56, 7.45) * mm});
            skPoint(sketch, "E37.25.20.0", {"position": v(23.38, 10.69) * mm});
            skLineSegment(sketch, "E37.26.20.0", {"start": v(25.52, 7) * mm, "end": v(26.3, 7.29) * mm});
            skLineSegment(sketch, "E37.29.20.0", {"start": v(26.9, 8.57) * mm, "end": v(26.14, 10.63) * mm});
            skPoint(sketch, "E37.0.21.0", {"position": v(23.4, 15.87) * mm});
            skArc(sketch, "E37.1.21.0", {"start": v(24.63, 11.74) * mm, "mid": v(25.1, 12.35) * mm, "end": v(25, 13.11) * mm});
            skLineSegment(sketch, "E37.5.21.0", {"start": v(22.54, 15.37) * mm, "end": v(21.82, 14.96) * mm});
            skArc(sketch, "E37.8.21.0", {"start": v(21.82, 14.96) * mm, "mid": v(21.47, 14.5) * mm, "end": v(21.55, 13.94) * mm});
            skArc(sketch, "E37.12.21.0", {"start": v(22.9, 11.6) * mm, "mid": v(23.35, 11.26) * mm, "end": v(23.92, 11.33) * mm});
            skPoint(sketch, "E37.16.21.0", {"position": v(23.27, 10.96) * mm});
            skArc(sketch, "E37.17.21.0", {"start": v(23.9, 15) * mm, "mid": v(23.3, 15.47) * mm, "end": v(22.54, 15.37) * mm});
            skPoint(sketch, "E37.21.21.0", {"position": v(25.5, 12.24) * mm});
            skLineSegment(sketch, "E37.22.21.0", {"start": v(21.55, 13.94) * mm, "end": v(22.9, 11.6) * mm});
            skPoint(sketch, "E37.25.21.0", {"position": v(21.17, 14.59) * mm});
            skLineSegment(sketch, "E37.26.21.0", {"start": v(23.92, 11.33) * mm, "end": v(24.63, 11.74) * mm});
            skLineSegment(sketch, "E37.29.21.0", {"start": v(25, 13.11) * mm, "end": v(23.9, 15) * mm});
            skPoint(sketch, "E37.0.22.0", {"position": v(20.29, 19.7) * mm});
            skArc(sketch, "E37.1.22.0", {"start": v(22.22, 15.84) * mm, "mid": v(22.57, 16.52) * mm, "end": v(22.34, 17.25) * mm});
            skLineSegment(sketch, "E37.5.22.0", {"start": v(19.52, 19.05) * mm, "end": v(18.9, 18.52) * mm});
            skArc(sketch, "E37.8.22.0", {"start": v(18.9, 18.52) * mm, "mid": v(18.63, 18.01) * mm, "end": v(18.8, 17.47) * mm});
            skArc(sketch, "E37.12.22.0", {"start": v(20.53, 15.4) * mm, "mid": v(21.04, 15.14) * mm, "end": v(21.59, 15.31) * mm});
            skPoint(sketch, "E37.16.22.0", {"position": v(21.01, 14.83) * mm});
            skArc(sketch, "E37.17.22.0", {"start": v(20.93, 18.93) * mm, "mid": v(20.25, 19.28) * mm, "end": v(19.52, 19.05) * mm});
            skPoint(sketch, "E37.21.22.0", {"position": v(22.98, 16.49) * mm});
            skLineSegment(sketch, "E37.22.22.0", {"start": v(18.8, 17.47) * mm, "end": v(20.53, 15.4) * mm});
            skPoint(sketch, "E37.25.22.0", {"position": v(18.32, 18.04) * mm});
            skLineSegment(sketch, "E37.26.22.0", {"start": v(21.59, 15.31) * mm, "end": v(22.22, 15.84) * mm});
            skLineSegment(sketch, "E37.29.22.0", {"start": v(22.34, 17.25) * mm, "end": v(20.93, 18.93) * mm});
            skPoint(sketch, "E37.0.23.0", {"position": v(16.56, 22.92) * mm});
            skArc(sketch, "E37.1.23.0", {"start": v(19.13, 19.46) * mm, "mid": v(19.36, 20.2) * mm, "end": v(19, 20.87) * mm});
            skLineSegment(sketch, "E37.5.23.0", {"start": v(15.92, 22.15) * mm, "end": v(15.39, 21.52) * mm});
            skArc(sketch, "E37.8.23.0", {"start": v(15.39, 21.52) * mm, "mid": v(15.22, 20.97) * mm, "end": v(15.48, 20.47) * mm});
            skArc(sketch, "E37.12.23.0", {"start": v(17.54, 18.74) * mm, "mid": v(18.09, 18.56) * mm, "end": v(18.6, 18.83) * mm});
            skPoint(sketch, "E37.16.23.0", {"position": v(18.12, 18.25) * mm});
            skArc(sketch, "E37.17.23.0", {"start": v(17.33, 22.28) * mm, "mid": v(16.6, 22.5) * mm, "end": v(15.92, 22.15) * mm});
            skPoint(sketch, "E37.21.23.0", {"position": v(19.77, 20.23) * mm});
            skLineSegment(sketch, "E37.22.23.0", {"start": v(15.48, 20.47) * mm, "end": v(17.54, 18.74) * mm});
            skPoint(sketch, "E37.25.23.0", {"position": v(14.9, 20.95) * mm});
            skLineSegment(sketch, "E37.26.23.0", {"start": v(18.6, 18.83) * mm, "end": v(19.13, 19.46) * mm});
            skLineSegment(sketch, "E37.29.23.0", {"start": v(19, 20.87) * mm, "end": v(17.33, 22.28) * mm});
            skPoint(sketch, "E37.0.24.0", {"position": v(12.33, 25.45) * mm});
            skArc(sketch, "E37.1.24.0", {"start": v(15.46, 22.49) * mm, "mid": v(15.56, 23.25) * mm, "end": v(15.1, 23.85) * mm});
            skLineSegment(sketch, "E37.5.24.0", {"start": v(11.83, 24.58) * mm, "end": v(11.42, 23.87) * mm});
            skArc(sketch, "E37.8.24.0", {"start": v(11.42, 23.87) * mm, "mid": v(11.34, 23.3) * mm, "end": v(11.7, 22.84) * mm});
            skArc(sketch, "E37.12.24.0", {"start": v(14.02, 21.5) * mm, "mid": v(14.6, 21.42) * mm, "end": v(15.05, 21.77) * mm});
            skPoint(sketch, "E37.16.24.0", {"position": v(14.67, 21.12) * mm});
            skArc(sketch, "E37.17.24.0", {"start": v(13.2, 24.95) * mm, "mid": v(12.44, 25.05) * mm, "end": v(11.83, 24.58) * mm});
            skPoint(sketch, "E37.21.24.0", {"position": v(15.96, 23.35) * mm});
            skLineSegment(sketch, "E37.22.24.0", {"start": v(11.7, 22.84) * mm, "end": v(14.02, 21.5) * mm});
            skPoint(sketch, "E37.25.24.0", {"position": v(11.04, 23.22) * mm});
            skLineSegment(sketch, "E37.26.24.0", {"start": v(15.05, 21.77) * mm, "end": v(15.46, 22.49) * mm});
            skLineSegment(sketch, "E37.29.24.0", {"start": v(15.1, 23.85) * mm, "end": v(13.2, 24.95) * mm});
            skPoint(sketch, "E37.0.25.0", {"position": v(7.72, 27.2) * mm});
            skArc(sketch, "E37.1.25.0", {"start": v(11.32, 24.83) * mm, "mid": v(11.29, 25.6) * mm, "end": v(10.72, 26.11) * mm});
            skLineSegment(sketch, "E37.5.25.0", {"start": v(7.38, 26.26) * mm, "end": v(7.1, 25.49) * mm});
            skArc(sketch, "E37.8.25.0", {"start": v(7.1, 25.49) * mm, "mid": v(7.12, 24.91) * mm, "end": v(7.55, 24.53) * mm});
            skArc(sketch, "E37.12.25.0", {"start": v(10.08, 23.6) * mm, "mid": v(10.65, 23.63) * mm, "end": v(11.04, 24.05) * mm});
            skPoint(sketch, "E37.16.25.0", {"position": v(10.78, 23.35) * mm});
            skArc(sketch, "E37.17.25.0", {"start": v(8.66, 26.86) * mm, "mid": v(7.9, 26.83) * mm, "end": v(7.38, 26.26) * mm});
            skPoint(sketch, "E37.21.25.0", {"position": v(11.66, 25.77) * mm});
            skLineSegment(sketch, "E37.22.25.0", {"start": v(7.55, 24.53) * mm, "end": v(10.08, 23.6) * mm});
            skPoint(sketch, "E37.25.25.0", {"position": v(6.84, 24.78) * mm});
            skLineSegment(sketch, "E37.26.25.0", {"start": v(11.04, 24.05) * mm, "end": v(11.32, 24.83) * mm});
            skLineSegment(sketch, "E37.29.25.0", {"start": v(10.72, 26.11) * mm, "end": v(8.66, 26.86) * mm});
            skPoint(sketch, "E37.0.26.0", {"position": v(2.88, 28.13) * mm});
            skArc(sketch, "E37.1.26.0", {"start": v(6.84, 26.42) * mm, "mid": v(6.67, 27.17) * mm, "end": v(6.02, 27.58) * mm});
            skLineSegment(sketch, "E37.5.26.0", {"start": v(2.7, 27.15) * mm, "end": v(2.57, 26.33) * mm});
            skArc(sketch, "E37.8.26.0", {"start": v(2.57, 26.33) * mm, "mid": v(2.69, 25.77) * mm, "end": v(3.17, 25.46) * mm});
            skArc(sketch, "E37.12.26.0", {"start": v(5.82, 25) * mm, "mid": v(6.38, 25.12) * mm, "end": v(6.7, 25.6) * mm});
            skPoint(sketch, "E37.16.26.0", {"position": v(6.56, 24.87) * mm});
            skArc(sketch, "E37.17.26.0", {"start": v(3.87, 27.96) * mm, "mid": v(3.12, 27.8) * mm, "end": v(2.7, 27.15) * mm});
            skPoint(sketch, "E37.21.26.0", {"position": v(7, 27.4) * mm});
            skLineSegment(sketch, "E37.22.26.0", {"start": v(3.17, 25.46) * mm, "end": v(5.82, 25) * mm});
            skPoint(sketch, "E37.25.26.0", {"position": v(2.43, 25.6) * mm});
            skLineSegment(sketch, "E37.26.26.0", {"start": v(6.7, 25.6) * mm, "end": v(6.84, 26.42) * mm});
            skLineSegment(sketch, "E37.29.26.0", {"start": v(6.02, 27.58) * mm, "end": v(3.87, 27.96) * mm});
            skPoint(sketch, "E37.0.27.0", {"position": v(-2.05, 28.2) * mm});
            skArc(sketch, "E37.1.27.0", {"start": v(2.14, 27.2) * mm, "mid": v(1.85, 27.91) * mm, "end": v(1.14, 28.2) * mm});
            skLineSegment(sketch, "E37.5.27.0", {"start": v(-2.05, 27.2) * mm, "end": v(-2.05, 26.38) * mm});
            skArc(sketch, "E37.8.27.0", {"start": v(-2.05, 26.38) * mm, "mid": v(-1.83, 25.85) * mm, "end": v(-1.3, 25.63) * mm});
            skArc(sketch, "E37.12.27.0", {"start": v(1.4, 25.63) * mm, "mid": v(1.92, 25.85) * mm, "end": v(2.14, 26.38) * mm});
            skPoint(sketch, "E37.16.27.0", {"position": v(2.14, 25.63) * mm});
            skArc(sketch, "E37.17.27.0", {"start": v(-1.05, 28.2) * mm, "mid": v(-1.75, 27.91) * mm, "end": v(-2.05, 27.2) * mm});
            skPoint(sketch, "E37.21.27.0", {"position": v(2.14, 28.2) * mm});
            skLineSegment(sketch, "E37.22.27.0", {"start": v(-1.3, 25.63) * mm, "end": v(1.4, 25.63) * mm});
            skPoint(sketch, "E37.25.27.0", {"position": v(-2.05, 25.63) * mm});
            skLineSegment(sketch, "E37.26.27.0", {"start": v(2.14, 26.38) * mm, "end": v(2.14, 27.2) * mm});
            skLineSegment(sketch, "E37.29.27.0", {"start": v(1.14, 28.2) * mm, "end": v(-1.05, 28.2) * mm});
            skPoint(sketch, "E37.0.28.0", {"position": v(-6.91, 27.42) * mm});
            skArc(sketch, "E37.1.28.0", {"start": v(-2.61, 27.16) * mm, "mid": v(-3.02, 27.8) * mm, "end": v(-3.77, 27.97) * mm});
            skLineSegment(sketch, "E37.5.28.0", {"start": v(-6.74, 26.43) * mm, "end": v(-6.6, 25.62) * mm});
            skArc(sketch, "E37.8.28.0", {"start": v(-6.6, 25.62) * mm, "mid": v(-6.29, 25.14) * mm, "end": v(-5.73, 25.01) * mm});
            skArc(sketch, "E37.12.28.0", {"start": v(-3.08, 25.48) * mm, "mid": v(-2.6, 25.79) * mm, "end": v(-2.47, 26.35) * mm});
            skPoint(sketch, "E37.16.28.0", {"position": v(-2.34, 25.61) * mm});
            skArc(sketch, "E37.17.28.0", {"start": v(-5.93, 27.6) * mm, "mid": v(-6.57, 27.18) * mm, "end": v(-6.74, 26.43) * mm});
            skPoint(sketch, "E37.21.28.0", {"position": v(-2.79, 28.15) * mm});
            skLineSegment(sketch, "E37.22.28.0", {"start": v(-5.73, 25.01) * mm, "end": v(-3.08, 25.48) * mm});
            skPoint(sketch, "E37.25.28.0", {"position": v(-6.47, 24.88) * mm});
            skLineSegment(sketch, "E37.26.28.0", {"start": v(-2.47, 26.35) * mm, "end": v(-2.61, 27.16) * mm});
            skLineSegment(sketch, "E37.29.28.0", {"start": v(-3.77, 27.97) * mm, "end": v(-5.93, 27.6) * mm});
            skPoint(sketch, "E37.0.29.0", {"position": v(-11.57, 25.8) * mm});
            skArc(sketch, "E37.1.29.0", {"start": v(-7.29, 26.3) * mm, "mid": v(-7.8, 26.86) * mm, "end": v(-8.57, 26.9) * mm});
            skLineSegment(sketch, "E37.5.29.0", {"start": v(-11.23, 24.86) * mm, "end": v(-10.94, 24.09) * mm});
            skArc(sketch, "E37.8.29.0", {"start": v(-10.94, 24.09) * mm, "mid": v(-10.56, 23.66) * mm, "end": v(-9.98, 23.64) * mm});
            skArc(sketch, "E37.12.29.0", {"start": v(-7.45, 24.56) * mm, "mid": v(-7.03, 24.95) * mm, "end": v(-7, 25.52) * mm});
            skPoint(sketch, "E37.16.29.0", {"position": v(-6.75, 24.82) * mm});
            skArc(sketch, "E37.17.29.0", {"start": v(-10.63, 26.14) * mm, "mid": v(-11.2, 25.63) * mm, "end": v(-11.23, 24.86) * mm});
            skPoint(sketch, "E37.21.29.0", {"position": v(-7.63, 27.24) * mm});
            skLineSegment(sketch, "E37.22.29.0", {"start": v(-9.98, 23.64) * mm, "end": v(-7.45, 24.56) * mm});
            skPoint(sketch, "E37.25.29.0", {"position": v(-10.69, 23.38) * mm});
            skLineSegment(sketch, "E37.26.29.0", {"start": v(-7, 25.52) * mm, "end": v(-7.29, 26.3) * mm});
            skLineSegment(sketch, "E37.29.29.0", {"start": v(-8.57, 26.9) * mm, "end": v(-10.63, 26.14) * mm});
            skPoint(sketch, "E37.0.30.0", {"position": v(-15.87, 23.4) * mm});
            skArc(sketch, "E37.1.30.0", {"start": v(-11.74, 24.63) * mm, "mid": v(-12.35, 25.1) * mm, "end": v(-13.11, 25) * mm});
            skLineSegment(sketch, "E37.5.30.0", {"start": v(-15.37, 22.54) * mm, "end": v(-14.96, 21.82) * mm});
            skArc(sketch, "E37.8.30.0", {"start": v(-14.96, 21.82) * mm, "mid": v(-14.5, 21.47) * mm, "end": v(-13.94, 21.55) * mm});
            skArc(sketch, "E37.12.30.0", {"start": v(-11.6, 22.9) * mm, "mid": v(-11.26, 23.35) * mm, "end": v(-11.33, 23.92) * mm});
            skPoint(sketch, "E37.16.30.0", {"position": v(-10.96, 23.27) * mm});
            skArc(sketch, "E37.17.30.0", {"start": v(-15, 23.9) * mm, "mid": v(-15.47, 23.3) * mm, "end": v(-15.37, 22.54) * mm});
            skPoint(sketch, "E37.21.30.0", {"position": v(-12.24, 25.5) * mm});
            skLineSegment(sketch, "E37.22.30.0", {"start": v(-13.94, 21.55) * mm, "end": v(-11.6, 22.9) * mm});
            skPoint(sketch, "E37.25.30.0", {"position": v(-14.59, 21.17) * mm});
            skLineSegment(sketch, "E37.26.30.0", {"start": v(-11.33, 23.92) * mm, "end": v(-11.74, 24.63) * mm});
            skLineSegment(sketch, "E37.29.30.0", {"start": v(-13.11, 25) * mm, "end": v(-15, 23.9) * mm});
            skPoint(sketch, "E37.0.31.0", {"position": v(-19.7, 20.29) * mm});
            skArc(sketch, "E37.1.31.0", {"start": v(-15.84, 22.22) * mm, "mid": v(-16.52, 22.57) * mm, "end": v(-17.25, 22.34) * mm});
            skLineSegment(sketch, "E37.5.31.0", {"start": v(-19.05, 19.52) * mm, "end": v(-18.52, 18.9) * mm});
            skArc(sketch, "E37.8.31.0", {"start": v(-18.52, 18.9) * mm, "mid": v(-18.01, 18.63) * mm, "end": v(-17.47, 18.8) * mm});
            skArc(sketch, "E37.12.31.0", {"start": v(-15.4, 20.53) * mm, "mid": v(-15.14, 21.04) * mm, "end": v(-15.31, 21.59) * mm});
            skPoint(sketch, "E37.16.31.0", {"position": v(-14.83, 21.01) * mm});
            skArc(sketch, "E37.17.31.0", {"start": v(-18.93, 20.93) * mm, "mid": v(-19.28, 20.25) * mm, "end": v(-19.05, 19.52) * mm});
            skPoint(sketch, "E37.21.31.0", {"position": v(-16.49, 22.98) * mm});
            skLineSegment(sketch, "E37.22.31.0", {"start": v(-17.47, 18.8) * mm, "end": v(-15.4, 20.53) * mm});
            skPoint(sketch, "E37.25.31.0", {"position": v(-18.04, 18.32) * mm});
            skLineSegment(sketch, "E37.26.31.0", {"start": v(-15.31, 21.59) * mm, "end": v(-15.84, 22.22) * mm});
            skLineSegment(sketch, "E37.29.31.0", {"start": v(-17.25, 22.34) * mm, "end": v(-18.93, 20.93) * mm});
            skPoint(sketch, "E37.0.32.0", {"position": v(-22.92, 16.56) * mm});
            skArc(sketch, "E37.1.32.0", {"start": v(-19.46, 19.13) * mm, "mid": v(-20.2, 19.36) * mm, "end": v(-20.87, 19) * mm});
            skLineSegment(sketch, "E37.5.32.0", {"start": v(-22.15, 15.92) * mm, "end": v(-21.52, 15.39) * mm});
            skArc(sketch, "E37.8.32.0", {"start": v(-21.52, 15.39) * mm, "mid": v(-20.97, 15.22) * mm, "end": v(-20.47, 15.48) * mm});
            skArc(sketch, "E37.12.32.0", {"start": v(-18.74, 17.54) * mm, "mid": v(-18.56, 18.09) * mm, "end": v(-18.83, 18.6) * mm});
            skPoint(sketch, "E37.16.32.0", {"position": v(-18.25, 18.12) * mm});
            skArc(sketch, "E37.17.32.0", {"start": v(-22.28, 17.33) * mm, "mid": v(-22.5, 16.6) * mm, "end": v(-22.15, 15.92) * mm});
            skPoint(sketch, "E37.21.32.0", {"position": v(-20.23, 19.77) * mm});
            skLineSegment(sketch, "E37.22.32.0", {"start": v(-20.47, 15.48) * mm, "end": v(-18.74, 17.54) * mm});
            skPoint(sketch, "E37.25.32.0", {"position": v(-20.95, 14.9) * mm});
            skLineSegment(sketch, "E37.26.32.0", {"start": v(-18.83, 18.6) * mm, "end": v(-19.46, 19.13) * mm});
            skLineSegment(sketch, "E37.29.32.0", {"start": v(-20.87, 19) * mm, "end": v(-22.28, 17.33) * mm});
            skPoint(sketch, "E37.0.33.0", {"position": v(-25.45, 12.33) * mm});
            skArc(sketch, "E37.1.33.0", {"start": v(-22.49, 15.46) * mm, "mid": v(-23.25, 15.56) * mm, "end": v(-23.85, 15.1) * mm});
            skLineSegment(sketch, "E37.5.33.0", {"start": v(-24.58, 11.83) * mm, "end": v(-23.87, 11.42) * mm});
            skArc(sketch, "E37.8.33.0", {"start": v(-23.87, 11.42) * mm, "mid": v(-23.3, 11.34) * mm, "end": v(-22.84, 11.7) * mm});
            skArc(sketch, "E37.12.33.0", {"start": v(-21.5, 14.02) * mm, "mid": v(-21.42, 14.6) * mm, "end": v(-21.77, 15.05) * mm});
            skPoint(sketch, "E37.16.33.0", {"position": v(-21.12, 14.67) * mm});
            skArc(sketch, "E37.17.33.0", {"start": v(-24.95, 13.2) * mm, "mid": v(-25.05, 12.44) * mm, "end": v(-24.58, 11.83) * mm});
            skPoint(sketch, "E37.21.33.0", {"position": v(-23.35, 15.96) * mm});
            skLineSegment(sketch, "E37.22.33.0", {"start": v(-22.84, 11.7) * mm, "end": v(-21.5, 14.02) * mm});
            skPoint(sketch, "E37.25.33.0", {"position": v(-23.22, 11.04) * mm});
            skLineSegment(sketch, "E37.26.33.0", {"start": v(-21.77, 15.05) * mm, "end": v(-22.49, 15.46) * mm});
            skLineSegment(sketch, "E37.29.33.0", {"start": v(-23.85, 15.1) * mm, "end": v(-24.95, 13.2) * mm});
            skPoint(sketch, "E37.0.34.0", {"position": v(-27.2, 7.72) * mm});
            skArc(sketch, "E37.1.34.0", {"start": v(-24.83, 11.32) * mm, "mid": v(-25.6, 11.29) * mm, "end": v(-26.11, 10.72) * mm});
            skLineSegment(sketch, "E37.5.34.0", {"start": v(-26.26, 7.38) * mm, "end": v(-25.49, 7.1) * mm});
            skArc(sketch, "E37.8.34.0", {"start": v(-25.49, 7.1) * mm, "mid": v(-24.91, 7.12) * mm, "end": v(-24.53, 7.55) * mm});
            skArc(sketch, "E37.12.34.0", {"start": v(-23.6, 10.08) * mm, "mid": v(-23.63, 10.65) * mm, "end": v(-24.05, 11.04) * mm});
            skPoint(sketch, "E37.16.34.0", {"position": v(-23.35, 10.78) * mm});
            skArc(sketch, "E37.17.34.0", {"start": v(-26.86, 8.66) * mm, "mid": v(-26.83, 7.9) * mm, "end": v(-26.26, 7.38) * mm});
            skPoint(sketch, "E37.21.34.0", {"position": v(-25.77, 11.66) * mm});
            skLineSegment(sketch, "E37.22.34.0", {"start": v(-24.53, 7.55) * mm, "end": v(-23.6, 10.08) * mm});
            skPoint(sketch, "E37.25.34.0", {"position": v(-24.78, 6.84) * mm});
            skLineSegment(sketch, "E37.26.34.0", {"start": v(-24.05, 11.04) * mm, "end": v(-24.83, 11.32) * mm});
            skLineSegment(sketch, "E37.29.34.0", {"start": v(-26.11, 10.72) * mm, "end": v(-26.86, 8.66) * mm});
            skPoint(sketch, "E37.0.35.0", {"position": v(-28.13, 2.88) * mm});
            skArc(sketch, "E37.1.35.0", {"start": v(-26.42, 6.84) * mm, "mid": v(-27.17, 6.67) * mm, "end": v(-27.58, 6.02) * mm});
            skLineSegment(sketch, "E37.5.35.0", {"start": v(-27.15, 2.7) * mm, "end": v(-26.33, 2.57) * mm});
            skArc(sketch, "E37.8.35.0", {"start": v(-26.33, 2.57) * mm, "mid": v(-25.77, 2.69) * mm, "end": v(-25.46, 3.17) * mm});
            skArc(sketch, "E37.12.35.0", {"start": v(-25, 5.82) * mm, "mid": v(-25.12, 6.38) * mm, "end": v(-25.6, 6.7) * mm});
            skPoint(sketch, "E37.16.35.0", {"position": v(-24.87, 6.56) * mm});
            skArc(sketch, "E37.17.35.0", {"start": v(-27.96, 3.87) * mm, "mid": v(-27.8, 3.12) * mm, "end": v(-27.15, 2.7) * mm});
            skPoint(sketch, "E37.21.35.0", {"position": v(-27.4, 7) * mm});
            skLineSegment(sketch, "E37.22.35.0", {"start": v(-25.46, 3.17) * mm, "end": v(-25, 5.82) * mm});
            skPoint(sketch, "E37.25.35.0", {"position": v(-25.6, 2.43) * mm});
            skLineSegment(sketch, "E37.26.35.0", {"start": v(-25.6, 6.7) * mm, "end": v(-26.42, 6.84) * mm});
            skLineSegment(sketch, "E37.29.35.0", {"start": v(-27.58, 6.02) * mm, "end": v(-27.96, 3.87) * mm});
            skSolve(sketch);
        }
        {
            var Q0;
            Q0 = qSketchRegion(id + "F6", true);
            extrude(context, id + "F7", {"entities" : qUnion([Q0]), "operationType" : NewBodyOperationType.REMOVE, "depth" : 1.5 * mm, "offsetDistance" : 25 * mm});
        }
        {
            var Q0;
            Q0=qCreatedBy(makeId("Top.planeOp"),FACE);
            cPlane(context, id + "F8", {"entities" : qUnion([Q0]), "cplaneType" : CPlaneType.OFFSET, "offset" : 1 * mm, "width" : 150 * mm, "height" : 150 * mm});
        }
        {
            var Q0;
            Q0=qCreatedBy(id+"F8.planeOp",FACE);
            var sketch = newSketch(context, id + "F9", { "sketchPlane" : qUnion([Q0])});
            skLineSegment(sketch, "E38.bottom", {"start": v(-33.9, -0.82) * mm, "end": v(-34.9, -0.82) * mm});
            skLineSegment(sketch, "E38.top", {"start": v(-33.9, 0.78) * mm, "end": v(-34.9, 0.78) * mm});
            skLineSegment(sketch, "E38.right", {"start": v(-34.9, -0.82) * mm, "end": v(-34.9, 0.78) * mm});
            skLineSegment(sketch, "E39.bottom", {"start": v(-34, -0.82) * mm, "end": v(-33.9, -0.82) * mm});
            skLineSegment(sketch, "E39.top", {"start": v(-34, 0.78) * mm, "end": v(-33.9, 0.78) * mm});
            skLineSegment(sketch, "E39.right", {"start": v(-33.5, -0.32) * mm, "end": v(-33.5, 0.28) * mm});
            skPoint(sketch, "E40.visualSharp", {"position": v(-33.5, 0.78) * mm});
            skArc(sketch, "E40.filletArc", {"start": v(-33.5, 0.28) * mm, "mid": v(-33.64, 0.64) * mm, "end": v(-34, 0.78) * mm});
            skPoint(sketch, "E41.visualSharp", {"position": v(-33.5, -0.82) * mm});
            skArc(sketch, "E41.filletArc", {"start": v(-34, -0.82) * mm, "mid": v(-33.64, -0.67) * mm, "end": v(-33.5, -0.32) * mm});
            skPoint(sketch, "E42.1.0", {"position": v(-24.24, -23.13) * mm});
            skPoint(sketch, "E42.1.1", {"position": v(-23.1, -24.26) * mm});
            skLineSegment(sketch, "E42.1.2", {"start": v(-23.4, -24.55) * mm, "end": v(-24.1, -25.26) * mm});
            skLineSegment(sketch, "E42.1.3", {"start": v(-24.53, -23.42) * mm, "end": v(-25.24, -24.13) * mm});
            skLineSegment(sketch, "E42.1.4", {"start": v(-24.1, -25.26) * mm, "end": v(-25.24, -24.13) * mm});
            skArc(sketch, "E42.1.5", {"start": v(-23.88, -23.48) * mm, "mid": v(-24.24, -23.34) * mm, "end": v(-24.59, -23.48) * mm});
            skLineSegment(sketch, "E42.1.6", {"start": v(-23.46, -24.62) * mm, "end": v(-23.4, -24.55) * mm});
            skLineSegment(sketch, "E42.1.7", {"start": v(-23.46, -23.9) * mm, "end": v(-23.88, -23.48) * mm});
            skArc(sketch, "E42.1.8", {"start": v(-23.46, -24.62) * mm, "mid": v(-23.31, -24.26) * mm, "end": v(-23.46, -23.9) * mm});
            skLineSegment(sketch, "E42.1.9", {"start": v(-24.59, -23.48) * mm, "end": v(-24.53, -23.42) * mm});
            skPoint(sketch, "E42.2.0", {"position": v(-0.78, -33.5) * mm});
            skPoint(sketch, "E42.2.1", {"position": v(0.82, -33.5) * mm});
            skLineSegment(sketch, "E42.2.2", {"start": v(0.82, -33.9) * mm, "end": v(0.82, -34.9) * mm});
            skLineSegment(sketch, "E42.2.3", {"start": v(-0.78, -33.9) * mm, "end": v(-0.78, -34.9) * mm});
            skLineSegment(sketch, "E42.2.4", {"start": v(0.82, -34.9) * mm, "end": v(-0.78, -34.9) * mm});
            skArc(sketch, "E42.2.5", {"start": v(-0.28, -33.5) * mm, "mid": v(-0.64, -33.64) * mm, "end": v(-0.78, -34) * mm});
            skLineSegment(sketch, "E42.2.6", {"start": v(0.82, -34) * mm, "end": v(0.82, -33.9) * mm});
            skLineSegment(sketch, "E42.2.7", {"start": v(0.32, -33.5) * mm, "end": v(-0.28, -33.5) * mm});
            skArc(sketch, "E42.2.8", {"start": v(0.82, -34) * mm, "mid": v(0.67, -33.64) * mm, "end": v(0.32, -33.5) * mm});
            skLineSegment(sketch, "E42.2.9", {"start": v(-0.78, -34) * mm, "end": v(-0.78, -33.9) * mm});
            skPoint(sketch, "E42.3.0", {"position": v(23.13, -24.24) * mm});
            skPoint(sketch, "E42.3.1", {"position": v(24.26, -23.1) * mm});
            skLineSegment(sketch, "E42.3.2", {"start": v(24.55, -23.4) * mm, "end": v(25.26, -24.1) * mm});
            skLineSegment(sketch, "E42.3.3", {"start": v(23.42, -24.53) * mm, "end": v(24.13, -25.24) * mm});
            skLineSegment(sketch, "E42.3.4", {"start": v(25.26, -24.1) * mm, "end": v(24.13, -25.24) * mm});
            skArc(sketch, "E42.3.5", {"start": v(23.48, -23.88) * mm, "mid": v(23.34, -24.24) * mm, "end": v(23.48, -24.59) * mm});
            skLineSegment(sketch, "E42.3.6", {"start": v(24.62, -23.46) * mm, "end": v(24.55, -23.4) * mm});
            skLineSegment(sketch, "E42.3.7", {"start": v(23.9, -23.46) * mm, "end": v(23.48, -23.88) * mm});
            skArc(sketch, "E42.3.8", {"start": v(24.62, -23.46) * mm, "mid": v(24.26, -23.31) * mm, "end": v(23.9, -23.46) * mm});
            skLineSegment(sketch, "E42.3.9", {"start": v(23.48, -24.59) * mm, "end": v(23.42, -24.53) * mm});
            skPoint(sketch, "E42.4.0", {"position": v(33.5, -0.78) * mm});
            skPoint(sketch, "E42.4.1", {"position": v(33.5, 0.82) * mm});
            skLineSegment(sketch, "E42.4.2", {"start": v(33.9, 0.82) * mm, "end": v(34.9, 0.82) * mm});
            skLineSegment(sketch, "E42.4.3", {"start": v(33.9, -0.78) * mm, "end": v(34.9, -0.78) * mm});
            skLineSegment(sketch, "E42.4.4", {"start": v(34.9, 0.82) * mm, "end": v(34.9, -0.78) * mm});
            skArc(sketch, "E42.4.5", {"start": v(33.5, -0.28) * mm, "mid": v(33.64, -0.64) * mm, "end": v(34, -0.78) * mm});
            skLineSegment(sketch, "E42.4.6", {"start": v(34, 0.82) * mm, "end": v(33.9, 0.82) * mm});
            skLineSegment(sketch, "E42.4.7", {"start": v(33.5, 0.32) * mm, "end": v(33.5, -0.28) * mm});
            skArc(sketch, "E42.4.8", {"start": v(34, 0.82) * mm, "mid": v(33.64, 0.67) * mm, "end": v(33.5, 0.32) * mm});
            skLineSegment(sketch, "E42.4.9", {"start": v(34, -0.78) * mm, "end": v(33.9, -0.78) * mm});
            skPoint(sketch, "E42.5.0", {"position": v(24.24, 23.13) * mm});
            skPoint(sketch, "E42.5.1", {"position": v(23.1, 24.26) * mm});
            skLineSegment(sketch, "E42.5.2", {"start": v(23.4, 24.55) * mm, "end": v(24.1, 25.26) * mm});
            skLineSegment(sketch, "E42.5.3", {"start": v(24.53, 23.42) * mm, "end": v(25.24, 24.13) * mm});
            skLineSegment(sketch, "E42.5.4", {"start": v(24.1, 25.26) * mm, "end": v(25.24, 24.13) * mm});
            skArc(sketch, "E42.5.5", {"start": v(23.88, 23.48) * mm, "mid": v(24.24, 23.34) * mm, "end": v(24.59, 23.48) * mm});
            skLineSegment(sketch, "E42.5.6", {"start": v(23.46, 24.62) * mm, "end": v(23.4, 24.55) * mm});
            skLineSegment(sketch, "E42.5.7", {"start": v(23.46, 23.9) * mm, "end": v(23.88, 23.48) * mm});
            skArc(sketch, "E42.5.8", {"start": v(23.46, 24.62) * mm, "mid": v(23.31, 24.26) * mm, "end": v(23.46, 23.9) * mm});
            skLineSegment(sketch, "E42.5.9", {"start": v(24.59, 23.48) * mm, "end": v(24.53, 23.42) * mm});
            skPoint(sketch, "E42.6.0", {"position": v(0.78, 33.5) * mm});
            skPoint(sketch, "E42.6.1", {"position": v(-0.82, 33.5) * mm});
            skLineSegment(sketch, "E42.6.2", {"start": v(-0.82, 33.9) * mm, "end": v(-0.82, 34.9) * mm});
            skLineSegment(sketch, "E42.6.3", {"start": v(0.78, 33.9) * mm, "end": v(0.78, 34.9) * mm});
            skLineSegment(sketch, "E42.6.4", {"start": v(-0.82, 34.9) * mm, "end": v(0.78, 34.9) * mm});
            skArc(sketch, "E42.6.5", {"start": v(0.28, 33.5) * mm, "mid": v(0.64, 33.64) * mm, "end": v(0.78, 34) * mm});
            skLineSegment(sketch, "E42.6.6", {"start": v(-0.82, 34) * mm, "end": v(-0.82, 33.9) * mm});
            skLineSegment(sketch, "E42.6.7", {"start": v(-0.32, 33.5) * mm, "end": v(0.28, 33.5) * mm});
            skArc(sketch, "E42.6.8", {"start": v(-0.82, 34) * mm, "mid": v(-0.67, 33.64) * mm, "end": v(-0.32, 33.5) * mm});
            skLineSegment(sketch, "E42.6.9", {"start": v(0.78, 34) * mm, "end": v(0.78, 33.9) * mm});
            skPoint(sketch, "E42.7.0", {"position": v(-23.13, 24.24) * mm});
            skPoint(sketch, "E42.7.1", {"position": v(-24.26, 23.1) * mm});
            skLineSegment(sketch, "E42.7.2", {"start": v(-24.55, 23.4) * mm, "end": v(-25.26, 24.1) * mm});
            skLineSegment(sketch, "E42.7.3", {"start": v(-23.42, 24.53) * mm, "end": v(-24.13, 25.24) * mm});
            skLineSegment(sketch, "E42.7.4", {"start": v(-25.26, 24.1) * mm, "end": v(-24.13, 25.24) * mm});
            skArc(sketch, "E42.7.5", {"start": v(-23.48, 23.88) * mm, "mid": v(-23.34, 24.24) * mm, "end": v(-23.48, 24.59) * mm});
            skLineSegment(sketch, "E42.7.6", {"start": v(-24.62, 23.46) * mm, "end": v(-24.55, 23.4) * mm});
            skLineSegment(sketch, "E42.7.7", {"start": v(-23.9, 23.46) * mm, "end": v(-23.48, 23.88) * mm});
            skArc(sketch, "E42.7.8", {"start": v(-24.62, 23.46) * mm, "mid": v(-24.26, 23.31) * mm, "end": v(-23.9, 23.46) * mm});
            skLineSegment(sketch, "E42.7.9", {"start": v(-23.48, 24.59) * mm, "end": v(-23.42, 24.53) * mm});
            skPoint(sketch, "E42.center", {"position": v(0, 0) * mm});
            skSolve(sketch);
        }
        {
            var Q0;
            Q0 = qSketchRegion(id + "F9", true);
            extrude(context, id + "F10", {"entities" : qUnion([Q0]), "operationType" : NewBodyOperationType.ADD, "depth" : 1.25 * mm, "offsetDistance" : 25 * mm, "hasDraft" : true, "draftAngle" : 5 * degree, "draftPullDirection" : true});
        }
        {
            var Q0;
            Q0=makeQuery(id+"F4.*.split.splitOp","SPLIT",BODY,{"derivedFrom":makeQuery(id+"F4.opExtrude","SWEPT_BODY",BODY,{"disambiguationData":[OSD([sQuery(id+"F3.wireOp",EDGE,"E18.bottom"),sQuery(id+"F3.wireOp",EDGE,"E18.top"),sQuery(id+"F3.wireOp",EDGE,"E18.left"),sQuery(id+"F3.wireOp",EDGE,"E18.right"),sQuery(id+"F3.wireOp",EDGE,"E19.filletArc"),sQuery(id+"F3.wireOp",EDGE,"E20.filletArc"),sQuery(id+"F3.wireOp",EDGE,"E21.filletArc"),sQuery(id+"F3.wireOp",EDGE,"E22.filletArc"),sQuery(id+"F3.wireOp",EDGE,"E26"),sQuery(id+"F3.wireOp",EDGE,"E27.left")])]})});
            var Q1;
            Q1=sQuery(id+"F0.wireOp",EDGE,"E1");
            circularPattern(context, id + "F11", {"entities" : qUnion([Q0]), "axis" : qUnion([Q1]), "angle" : 360 * degree, "instanceCount" : 4, "equalSpace" : true});
        }
        {
            var Q0;
            Q0=makeQuery(id+"F10.opExtrude","CAP_EDGE",EDGE,{"disambiguationData":[OSD([sQuery(id+"F9.wireOp",EDGE,"E39.right")])],"isStart":true});
            var Q1;
            Q1=makeQuery(id+"F10.opExtrude","CAP_EDGE",EDGE,{"disambiguationData":[OSD([sQuery(id+"F9.wireOp",EDGE,"E42.7.7")])],"isStart":true});
            var Q2;
            Q2=makeQuery(id+"F10.opExtrude","CAP_EDGE",EDGE,{"disambiguationData":[OSD([sQuery(id+"F9.wireOp",EDGE,"E42.6.7")])],"isStart":true});
            var Q3;
            Q3=makeQuery(id+"F10.opExtrude","CAP_EDGE",EDGE,{"disambiguationData":[OSD([sQuery(id+"F9.wireOp",EDGE,"E42.5.7")])],"isStart":true});
            var Q4;
            Q4=makeQuery(id+"F10.opExtrude","CAP_EDGE",EDGE,{"disambiguationData":[OSD([sQuery(id+"F9.wireOp",EDGE,"E42.4.7")])],"isStart":true});
            var Q5;
            Q5=makeQuery(id+"F10.opExtrude","CAP_EDGE",EDGE,{"disambiguationData":[OSD([sQuery(id+"F9.wireOp",EDGE,"E42.3.7")])],"isStart":true});
            var Q6;
            Q6=makeQuery(id+"F10.opExtrude","CAP_EDGE",EDGE,{"disambiguationData":[OSD([sQuery(id+"F9.wireOp",EDGE,"E42.2.7")])],"isStart":true});
            var Q7;
            Q7=makeQuery(id+"F10.opExtrude","CAP_EDGE",EDGE,{"disambiguationData":[OSD([sQuery(id+"F9.wireOp",EDGE,"E42.1.7")])],"isStart":true});
            chamfer(context, id + "F12", {"entities" : qUnion([Q0, Q1, Q2, Q3, Q4, Q5, Q6, Q7]), "chamferType" : ChamferType.OFFSET_ANGLE, "width" : .4 * mm, "oppositeDirection" : false, "angle" : 40 * degree});
        }
        {
            var Q0;
            Q0=makeQuery(id+"F10.opExtrude","CAP_EDGE",EDGE,{"disambiguationData":[OSD([sQuery(id+"F9.wireOp",EDGE,"E39.right")])],"isStart":false});
            var Q1;
            Q1=makeQuery(id+"F10.opExtrude","CAP_EDGE",EDGE,{"disambiguationData":[OSD([sQuery(id+"F9.wireOp",EDGE,"E42.7.7")])],"isStart":false});
            var Q2;
            Q2=makeQuery(id+"F10.opExtrude","CAP_EDGE",EDGE,{"disambiguationData":[OSD([sQuery(id+"F9.wireOp",EDGE,"E42.6.7")])],"isStart":false});
            var Q3;
            Q3=makeQuery(id+"F10.opExtrude","CAP_EDGE",EDGE,{"disambiguationData":[OSD([sQuery(id+"F9.wireOp",EDGE,"E42.2.7")])],"isStart":false});
            var Q4;
            Q4=makeQuery(id+"F10.opExtrude","CAP_EDGE",EDGE,{"disambiguationData":[OSD([sQuery(id+"F9.wireOp",EDGE,"E42.4.7")])],"isStart":false});
            var Q5;
            Q5=makeQuery(id+"F10.opExtrude","CAP_EDGE",EDGE,{"disambiguationData":[OSD([sQuery(id+"F9.wireOp",EDGE,"E42.3.7")])],"isStart":false});
            var Q6;
            Q6=makeQuery(id+"F10.opExtrude","CAP_EDGE",EDGE,{"disambiguationData":[OSD([sQuery(id+"F9.wireOp",EDGE,"E42.5.7")])],"isStart":false});
            var Q7;
            Q7=makeQuery(id+"F10.opExtrude","CAP_EDGE",EDGE,{"disambiguationData":[OSD([sQuery(id+"F9.wireOp",EDGE,"E42.1.7")])],"isStart":false});
            fillet(context, id + "F13", {"entities" : qUnion([Q0, Q1, Q2, Q3, Q4, Q5, Q6, Q7]), "radius" : .7 * mm, "tangentPropagation" : true, "rho" : 0.1, "crossSection" : FilletCrossSection.CONIC, "allowEdgeOverflow" : false});
        }
    });
